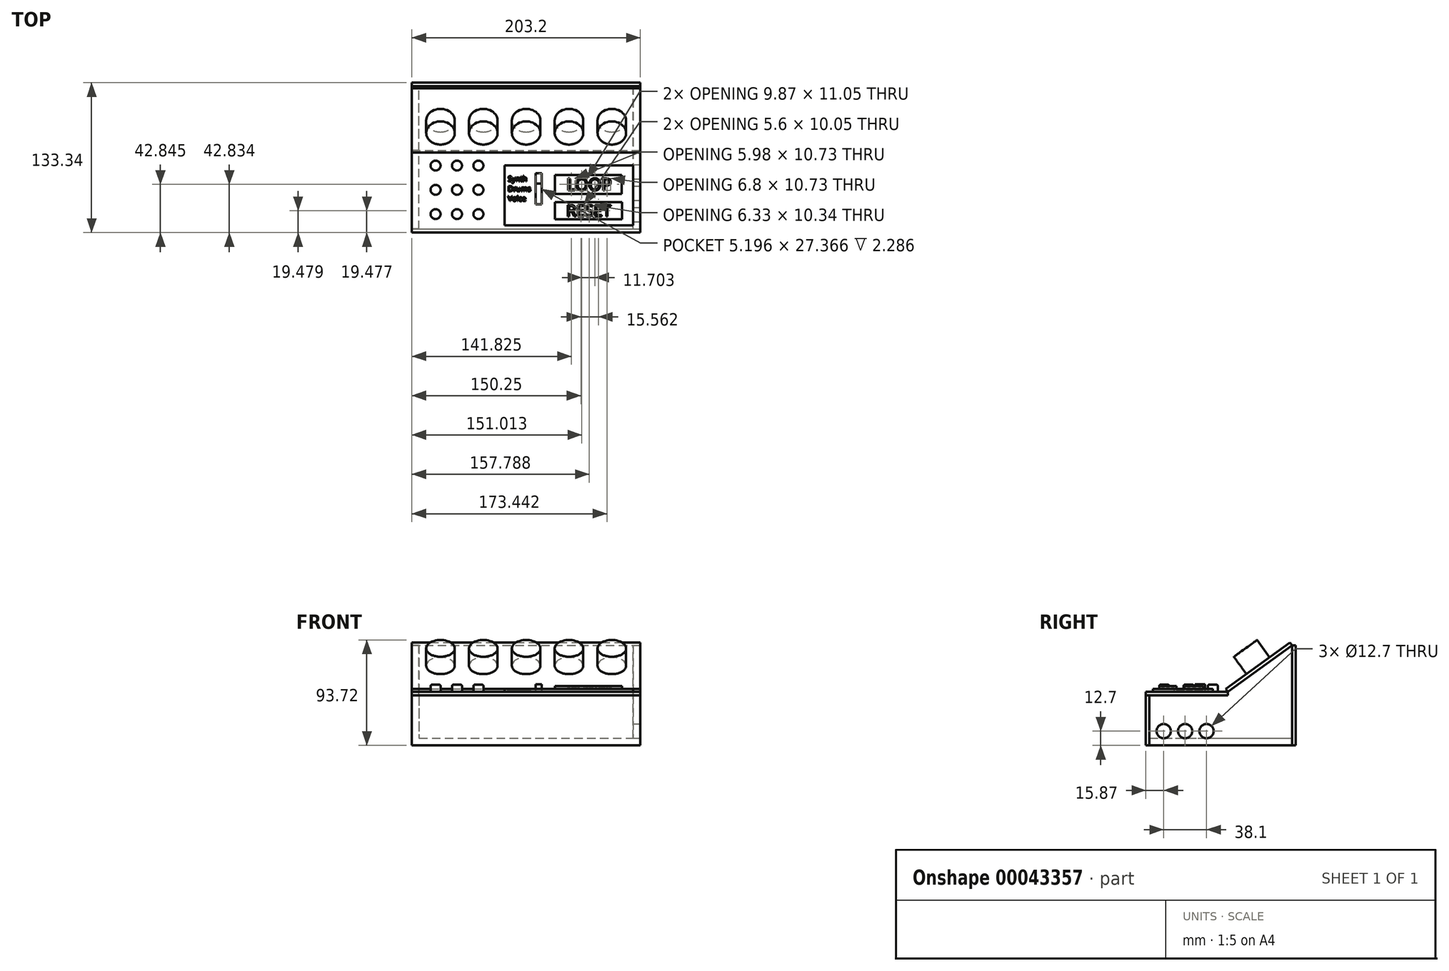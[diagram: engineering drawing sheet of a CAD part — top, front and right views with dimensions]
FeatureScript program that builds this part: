
annotation { "Feature Type Name" : "Feature", "Feature Type Description" : "" }
export const myFeature = defineFeature(function(context is Context, id is Id, definition is map)
    precondition{}
    {
        {
            var Q0;
            Q0=qCreatedBy(makeId("Top.planeOp"),FACE);
            var sketch = newSketch(context, id + "F0", { "sketchPlane" : qUnion([Q0])});
            skLineSegment(sketch, "E0.rect.bottom", {"start": v(-101.6, -63.5) * mm, "end": v(101.6, -63.5) * mm});
            skLineSegment(sketch, "E0.rect.top", {"start": v(-101.6, 63.5) * mm, "end": v(101.6, 63.5) * mm});
            skLineSegment(sketch, "E0.rect.left", {"start": v(-101.6, -63.5) * mm, "end": v(-101.6, 63.5) * mm});
            skLineSegment(sketch, "E0.rect.right", {"start": v(101.6, -63.5) * mm, "end": v(101.6, 63.5) * mm});
            skPoint(sketch, "E0.rect.middle", {"position": v(0, 0) * mm});
            skSolve(sketch);
        }
        {
            var Q0;
            Q0 = qSketchRegion(id + "F0", true);
            extrude(context, id + "F1", {"entities" : qUnion([Q0]), "depth" : 6.35 * mm});
        }
        {
            var Q0;
            Q0=makeQuery(id+"F1.opExtrude","SWEPT_FACE",FACE,{"disambiguationData":[OSD([sQuery(id+"F0.wireOp",EDGE,"E0.rect.left")])]});
            var sketch = newSketch(context, id + "F2", { "sketchPlane" : qUnion([Q0])});
            skLineSegment(sketch, "E1", {"start": v(-63.5, 6.35) * mm, "end": v(0, 6.35) * mm});
            skLineSegment(sketch, "E2", {"start": v(0, 6.35) * mm, "end": v(0, 44.45) * mm});
            skLineSegment(sketch, "E3", {"start": v(0, 44.45) * mm, "end": v(-6.35, 44.45) * mm});
            skLineSegment(sketch, "E4", {"start": v(-6.35, 44.45) * mm, "end": v(-6.35, 47.63) * mm});
            skLineSegment(sketch, "E5", {"start": v(-6.35, 47.62) * mm, "end": v(-63.5, 88.9) * mm});
            skLineSegment(sketch, "E6", {"start": v(-63.5, 88.9) * mm, "end": v(-63.5, 6.35) * mm});
            skLineSegment(sketch, "E7", {"start": v(0, 44.45) * mm, "end": v(63.5, 44.45) * mm});
            skLineSegment(sketch, "E8", {"start": v(63.5, 44.45) * mm, "end": v(63.5, 6.35) * mm});
            skLineSegment(sketch, "E9", {"start": v(63.5, 6.35) * mm, "end": v(0, 6.35) * mm});
            skSolve(sketch);
        }
        {
            var Q0;
            Q0 = qSketchRegion(id + "F2", true);
            extrude(context, id + "F3", {"entities" : qUnion([Q0]), "operationType" : NewBodyOperationType.ADD, "oppositeDirection" : true, "depth" : 6.35 * mm});
        }
        {
            var Q0;
            Q0=makeQuery(id+"F1.opExtrude","SWEPT_FACE",FACE,{"disambiguationData":[OSD([sQuery(id+"F0.wireOp",EDGE,"E0.rect.right")])]});
            var sketch = newSketch(context, id + "F4", { "sketchPlane" : qUnion([Q0])});
            skLineSegment(sketch, "E10.0.0", {"start": v(63.5, 6.35) * mm, "end": v(63.5, 6.35) * mm});
            skLineSegment(sketch, "E11.0.0", {"start": v(-63.5, 6.35) * mm, "end": v(63.5, 6.35) * mm});
            skLineSegment(sketch, "E11.0.1", {"start": v(63.5, 6.35) * mm, "end": v(63.5, 88.9) * mm});
            skLineSegment(sketch, "E11.0.2", {"start": v(63.5, 88.9) * mm, "end": v(6.35, 47.62) * mm});
            skLineSegment(sketch, "E11.0.3", {"start": v(6.35, 47.62) * mm, "end": v(6.35, 44.45) * mm});
            skLineSegment(sketch, "E11.0.4", {"start": v(6.35, 44.45) * mm, "end": v(-63.5, 44.45) * mm});
            skLineSegment(sketch, "E11.0.5", {"start": v(-63.5, 44.45) * mm, "end": v(-63.5, 6.35) * mm});
            skSolve(sketch);
        }
        {
            var Q0;
            Q0 = qSketchRegion(id + "F4", true);
            extrude(context, id + "F5", {"entities" : qUnion([Q0]), "operationType" : NewBodyOperationType.ADD, "oppositeDirection" : true, "depth" : 6.35 * mm});
        }
        {
            var Q0;
            Q0=makeQuery(id+"F3.opExtrude","SWEPT_FACE",FACE,{"disambiguationData":[OSD([sQuery(id+"F2.wireOp",EDGE,"E5")])]});
            var sketch = newSketch(context, id + "F6", { "sketchPlane" : qUnion([Q0])});
            skLineSegment(sketch, "E12", {"start": v(-101.6, 103.53) * mm, "end": v(101.6, 103.53) * mm});
            skLineSegment(sketch, "E13", {"start": v(-101.6, 103.53) * mm, "end": v(-101.6, 33.03) * mm});
            skLineSegment(sketch, "E14", {"start": v(-101.6, 33.03) * mm, "end": v(101.6, 33.03) * mm});
            skLineSegment(sketch, "E15", {"start": v(101.6, 33.03) * mm, "end": v(101.6, 103.53) * mm});
            skSolve(sketch);
        }
        {
            var Q0;
            Q0 = qSketchRegion(id + "F6", true);
            extrude(context, id + "F7", {"entities" : qUnion([Q0]), "depth" : 3.17 * mm});
        }
        {
            var Q0;
            Q0=makeQuery(id+"F3.opExtrude","SWEPT_FACE",FACE,{"disambiguationData":[OSD([sQuery(id+"F2.wireOp",EDGE,"E3"),sQuery(id+"F2.wireOp",EDGE,"E7")])]});
            var sketch = newSketch(context, id + "F8", { "sketchPlane" : qUnion([Q0])});
            skLineSegment(sketch, "E16", {"start": v(-101.6, 6.35) * mm, "end": v(101.6, 6.35) * mm});
            skLineSegment(sketch, "E17", {"start": v(101.6, 6.35) * mm, "end": v(101.6, -63.5) * mm});
            skLineSegment(sketch, "E18", {"start": v(-101.6, 6.35) * mm, "end": v(-101.6, -66.68) * mm});
            skLineSegment(sketch, "E19", {"start": v(-101.6, -66.68) * mm, "end": v(101.6, -66.67) * mm});
            skLineSegment(sketch, "E20", {"start": v(101.6, -66.67) * mm, "end": v(101.6, -63.5) * mm});
            skSolve(sketch);
        }
        {
            var Q0;
            Q0 = qSketchRegion(id + "F8", true);
            extrude(context, id + "F9", {"entities" : qUnion([Q0]), "depth" : 3.17 * mm});
        }
        {
            var Q0;
            Q0=makeQuery(id+"F5.boolean.opBoolean","MERGE",FACE,{"derivedFrom":[makeQuery(id+"F3.boolean.opBoolean","MERGE",FACE,{"derivedFrom":[makeQuery(id+"F1.opExtrude","SWEPT_FACE",FACE,{"disambiguationData":[OSD([sQuery(id+"F0.wireOp",EDGE,"E0.rect.bottom")])]}),makeQuery(id+"F3.opExtrude","SWEPT_FACE",FACE,{"disambiguationData":[OSD([sQuery(id+"F2.wireOp",EDGE,"E8")])]})]}),makeQuery(id+"F5.opExtrude","SWEPT_FACE",FACE,{"disambiguationData":[OSD([sQuery(id+"F4.wireOp",EDGE,"E11.0.5")])]})]});
            var sketch = newSketch(context, id + "F10", { "sketchPlane" : qUnion([Q0])});
            skLineSegment(sketch, "E21.bottom", {"start": v(-101.6, 0) * mm, "end": v(101.6, 0) * mm});
            skLineSegment(sketch, "E21.top", {"start": v(-101.6, 44.45) * mm, "end": v(101.6, 44.45) * mm});
            skLineSegment(sketch, "E21.left", {"start": v(-101.6, 0) * mm, "end": v(-101.6, 44.45) * mm});
            skLineSegment(sketch, "E21.right", {"start": v(101.6, 0) * mm, "end": v(101.6, 44.45) * mm});
            skSolve(sketch);
        }
        {
            var Q0;
            Q0 = qSketchRegion(id + "F10", true);
            extrude(context, id + "F11", {"entities" : qUnion([Q0]), "depth" : 3.17 * mm});
        }
        {
            var Q0;
            Q0=makeQuery(id+"F5.boolean.opBoolean","MERGE",FACE,{"derivedFrom":[makeQuery(id+"F3.boolean.opBoolean","MERGE",FACE,{"derivedFrom":[makeQuery(id+"F1.opExtrude","SWEPT_FACE",FACE,{"disambiguationData":[OSD([sQuery(id+"F0.wireOp",EDGE,"E0.rect.top")])]}),makeQuery(id+"F3.opExtrude","SWEPT_FACE",FACE,{"disambiguationData":[OSD([sQuery(id+"F2.wireOp",EDGE,"E6")])]})]}),makeQuery(id+"F5.opExtrude","SWEPT_FACE",FACE,{"disambiguationData":[OSD([sQuery(id+"F4.wireOp",EDGE,"E11.0.1")])]})]});
            var sketch = newSketch(context, id + "F12", { "sketchPlane" : qUnion([Q0])});
            skLineSegment(sketch, "E22.bottom", {"start": v(-101.6, 0) * mm, "end": v(101.6, 0) * mm});
            skLineSegment(sketch, "E22.top", {"start": v(-101.6, 88.9) * mm, "end": v(101.6, 88.9) * mm});
            skLineSegment(sketch, "E22.left", {"start": v(-101.6, 0) * mm, "end": v(-101.6, 88.9) * mm});
            skLineSegment(sketch, "E22.right", {"start": v(101.6, 0) * mm, "end": v(101.6, 88.9) * mm});
            skSolve(sketch);
        }
        {
            var Q0;
            Q0 = qSketchRegion(id + "F12", true);
            extrude(context, id + "F13", {"entities" : qUnion([Q0]), "depth" : 3.17 * mm});
        }
        {
            var Q0;
            Q0=makeQuery(id+"F7.opExtrude","CAP_FACE",FACE,{"disambiguationData":[OSD([sQuery(id+"F6.wireOp",EDGE,"E12"),sQuery(id+"F6.wireOp",EDGE,"E13"),sQuery(id+"F6.wireOp",EDGE,"E14"),sQuery(id+"F6.wireOp",EDGE,"E15")])],"isStart":false});
            var sketch = newSketch(context, id + "F14", { "sketchPlane" : qUnion([Q0])});
            skCircle(sketch, "E23", {"center": v(76.2, 68.28) * mm, "radius": 12.7 * mm});
            skPoint(sketch, "E23.centerSnap0", {"position": v(101.6, 68.28) * mm});
            skCircle(sketch, "E24", {"center": v(38.1, 68.28) * mm, "radius": 12.7 * mm});
            skCircle(sketch, "E25", {"center": v(0, 68.28) * mm, "radius": 12.7 * mm});
            skCircle(sketch, "E26", {"center": v(-38.1, 68.28) * mm, "radius": 12.7 * mm});
            skCircle(sketch, "E27", {"center": v(-76.2, 68.28) * mm, "radius": 12.7 * mm});
            skSolve(sketch);
        }
        {
            var Q0;
            Q0 = qSketchRegion(id + "F14", true);
            extrude(context, id + "F15", {"entities" : qUnion([Q0]), "depth" : 19.05 * mm});
        }
        {
            var Q0;
            Q0=makeQuery(id+"F5.boolean.opBoolean","MERGE",FACE,{"derivedFrom":[makeQuery(id+"F1.opExtrude","SWEPT_FACE",FACE,{"disambiguationData":[OSD([sQuery(id+"F0.wireOp",EDGE,"E0.rect.right")])]}),makeQuery(id+"F5.opExtrude","CAP_FACE",FACE,{"disambiguationData":[OSD([sQuery(id+"F4.wireOp",EDGE,"E11.0.0"),sQuery(id+"F4.wireOp",EDGE,"E11.0.1"),sQuery(id+"F4.wireOp",EDGE,"E11.0.2"),sQuery(id+"F4.wireOp",EDGE,"E11.0.3"),sQuery(id+"F4.wireOp",EDGE,"E11.0.4"),sQuery(id+"F4.wireOp",EDGE,"E11.0.5")])],"isStart":true})]});
            var sketch = newSketch(context, id + "F16", { "sketchPlane" : qUnion([Q0])});
            skCircle(sketch, "E28", {"center": v(-50.8, 12.7) * mm, "radius": 6.35 * mm});
            skCircle(sketch, "E29", {"center": v(-31.75, 12.7) * mm, "radius": 6.35 * mm});
            skCircle(sketch, "E30", {"center": v(-12.7, 12.7) * mm, "radius": 6.35 * mm});
            skSolve(sketch);
        }
        {
            var Q0;
            Q0 = qSketchRegion(id + "F16", true);
            extrude(context, id + "F17", {"entities" : qUnion([Q0]), "operationType" : NewBodyOperationType.REMOVE, "oppositeDirection" : true, "depth" : 25.4 * mm});
        }
        {
            var Q0;
            Q0=makeQuery(id+"F9.opExtrude","CAP_FACE",FACE,{"disambiguationData":[OSD([sQuery(id+"F8.wireOp",EDGE,"E16"),sQuery(id+"F8.wireOp",EDGE,"E17"),sQuery(id+"F8.wireOp",EDGE,"E18"),sQuery(id+"F8.wireOp",EDGE,"E19"),sQuery(id+"F8.wireOp",EDGE,"E20")])],"isStart":false});
            var sketch = newSketch(context, id + "F18", { "sketchPlane" : qUnion([Q0])});
            skCircle(sketch, "E31", {"center": v(-63.5, -34.93) * mm, "radius": 26.07 * mm});
            skSolve(sketch);
        }
        {
            var Q0;
            Q0 = qSketchRegion(id + "F18", true);
            extrude(context, id + "F19", {"entities" : qUnion([Q0]), "depth" : 6.35 * mm});
        }
        {
            var Q0;
            Q0=makeQuery(id+"F19.opExtrude","CAP_EDGE",EDGE,{"disambiguationData":[OSD([sQuery(id+"F18.wireOp",EDGE,"E31")])],"isStart":false});
            fillet(context, id + "F20", {"entities" : qUnion([Q0]), "radius" : 6.35 * mm, "tangentPropagation" : true, "allowEdgeOverflow" : false});
        }
        {
            var Q0;
            Q0=makeQuery(id+"F9.opExtrude","CAP_FACE",FACE,{"disambiguationData":[OSD([sQuery(id+"F8.wireOp",EDGE,"E16"),sQuery(id+"F8.wireOp",EDGE,"E17"),sQuery(id+"F8.wireOp",EDGE,"E18"),sQuery(id+"F8.wireOp",EDGE,"E19"),sQuery(id+"F8.wireOp",EDGE,"E20")])],"isStart":false});
            var sketch = newSketch(context, id + "F21", { "sketchPlane" : qUnion([Q0])});
            skLineSegment(sketch, "E32.rect.bottom", {"start": v(95.25, -60.32) * mm, "end": v(-19.05, -60.32) * mm});
            skLineSegment(sketch, "E32.rect.top", {"start": v(95.25, -6.98) * mm, "end": v(-19.05, -6.98) * mm});
            skLineSegment(sketch, "E32.rect.left", {"start": v(95.25, -60.32) * mm, "end": v(95.25, -6.98) * mm});
            skLineSegment(sketch, "E32.rect.right", {"start": v(-19.05, -60.32) * mm, "end": v(-19.05, -6.98) * mm});
            skPoint(sketch, "E32.rect.middle", {"position": v(38.1, -33.65) * mm});
            skSolve(sketch);
        }
        {
            var Q0;
            Q0 = qSketchRegion(id + "F21", true);
            extrude(context, id + "F22", {"entities" : qUnion([Q0]), "operationType" : NewBodyOperationType.ADD, "depth" : 2.54 * mm});
        }
        {
            var Q0;
            Q0=makeQuery(id+"F22.opExtrude","CAP_FACE",FACE,{"disambiguationData":[OSD([sQuery(id+"F21.wireOp",EDGE,"E32.rect.bottom"),sQuery(id+"F21.wireOp",EDGE,"E32.rect.top"),sQuery(id+"F21.wireOp",EDGE,"E32.rect.left"),sQuery(id+"F21.wireOp",EDGE,"E32.rect.right")])],"isStart":false});
            var sketch = newSketch(context, id + "F23", { "sketchPlane" : qUnion([Q0])});
            skText(sketch, "E33", { "text": "Synth\nDrums\nVoice", "fontName": "OpenSans-Regular.ttf"});
            const initialGuessF23  = {"E33": [-0.0162, -0.02115, 1, 0, 0.00466]};
            skSetInitialGuess(sketch, initialGuessF23);
            skSolve(sketch);
        }
        {
            var Q0;
            Q0 = qSketchRegion(id + "F23", true);
            extrude(context, id + "F24", {"entities" : qUnion([Q0]), "operationType" : NewBodyOperationType.REMOVE, "oppositeDirection" : true, "depth" : 1.27 * mm});
        }
        {
            var Q0;
            {var subQ0=sQuery(id+"F21.wireOp",EDGE,"E32.rect.bottom");var subQ1=sQuery(id+"F21.wireOp",EDGE,"E32.rect.top");var subQ2=sQuery(id+"F21.wireOp",EDGE,"E32.rect.left");var subQ3=sQuery(id+"F21.wireOp",EDGE,"E32.rect.right");Q0=makeQuery(id+"F24.boolean.opBoolean","SPLIT",FACE,{"disambiguationData":[TD([makeQuery(id+"F22.opExtrude","SWEPT_FACE",FACE,{"disambiguationData":[OSD([subQ0])]})])],"derivedFrom":makeQuery(id+"F22.opExtrude","CAP_FACE",FACE,{"disambiguationData":[OSD([subQ0,subQ1,subQ2,subQ3])],"isStart":false})});}
            var sketch = newSketch(context, id + "F25", { "sketchPlane" : qUnion([Q0])});
            skLineSegment(sketch, "E34.rect.bottom", {"start": v(8.48, -14.05) * mm, "end": v(13.67, -14.05) * mm});
            skLineSegment(sketch, "E34.rect.top", {"start": v(8.48, -41.41) * mm, "end": v(13.67, -41.41) * mm});
            skLineSegment(sketch, "E34.rect.left", {"start": v(8.48, -14.05) * mm, "end": v(8.48, -41.41) * mm});
            skLineSegment(sketch, "E34.rect.right", {"start": v(13.67, -14.05) * mm, "end": v(13.67, -41.41) * mm});
            skPoint(sketch, "E34.rect.middle", {"position": v(11.08, -27.73) * mm});
            skSolve(sketch);
        }
        {
            var Q0;
            Q0 = qSketchRegion(id + "F25", true);
            extrude(context, id + "F26", {"entities" : qUnion([Q0]), "operationType" : NewBodyOperationType.REMOVE, "oppositeDirection" : true, "depth" : 2.3 * mm});
        }
        {
            var Q0;
            Q0=makeQuery(id+"F26.boolean.opBoolean","COPY",FACE,{"derivedFrom":makeQuery(id+"F26.opExtrude","CAP_FACE",FACE,{"disambiguationData":[OSD([sQuery(id+"F25.wireOp",EDGE,"E34.rect.bottom"),sQuery(id+"F25.wireOp",EDGE,"E34.rect.top"),sQuery(id+"F25.wireOp",EDGE,"E34.rect.left"),sQuery(id+"F25.wireOp",EDGE,"E34.rect.right")])],"isStart":false})});
            var sketch = newSketch(context, id + "F27", { "sketchPlane" : qUnion([Q0])});
            skLineSegment(sketch, "E35.bottom", {"start": v(8.48, -14.05) * mm, "end": v(13.67, -14.05) * mm});
            skLineSegment(sketch, "E35.top", {"start": v(8.48, -23.05) * mm, "end": v(13.67, -23.05) * mm});
            skLineSegment(sketch, "E35.left", {"start": v(8.48, -14.05) * mm, "end": v(8.48, -23.05) * mm});
            skLineSegment(sketch, "E35.right", {"start": v(13.67, -14.05) * mm, "end": v(13.67, -23.05) * mm});
            skSolve(sketch);
        }
        {
            var Q0;
            Q0 = qSketchRegion(id + "F27", true);
            extrude(context, id + "F28", {"entities" : qUnion([Q0]), "depth" : 6.35 * mm});
        }
        {
            var Q0;
            {var subQ0=sQuery(id+"F21.wireOp",EDGE,"E32.rect.bottom");var subQ1=sQuery(id+"F21.wireOp",EDGE,"E32.rect.top");var subQ2=sQuery(id+"F21.wireOp",EDGE,"E32.rect.left");var subQ3=sQuery(id+"F21.wireOp",EDGE,"E32.rect.right");Q0=makeQuery(id+"F24.boolean.opBoolean","SPLIT",FACE,{"disambiguationData":[TD([makeQuery(id+"F22.opExtrude","SWEPT_FACE",FACE,{"disambiguationData":[OSD([subQ0])]})])],"derivedFrom":makeQuery(id+"F22.opExtrude","CAP_FACE",FACE,{"disambiguationData":[OSD([subQ0,subQ1,subQ2,subQ3])],"isStart":false})});}
            var sketch = newSketch(context, id + "F29", { "sketchPlane" : qUnion([Q0])});
            skLineSegment(sketch, "E36.bottom", {"start": v(25.45, -15.63) * mm, "end": v(85.06, -15.63) * mm});
            skLineSegment(sketch, "E36.top", {"start": v(25.45, -32.46) * mm, "end": v(85.06, -32.46) * mm});
            skLineSegment(sketch, "E36.left", {"start": v(25.45, -15.63) * mm, "end": v(25.45, -32.46) * mm});
            skLineSegment(sketch, "E36.right", {"start": v(85.06, -15.63) * mm, "end": v(85.06, -32.46) * mm});
            skLineSegment(sketch, "E37.bottom", {"start": v(25.45, -39.5) * mm, "end": v(85.4, -39.5) * mm});
            skLineSegment(sketch, "E37.top", {"start": v(25.45, -54.8) * mm, "end": v(85.4, -54.8) * mm});
            skLineSegment(sketch, "E37.left", {"start": v(25.45, -39.5) * mm, "end": v(25.45, -54.8) * mm});
            skLineSegment(sketch, "E37.right", {"start": v(85.4, -39.5) * mm, "end": v(85.4, -54.8) * mm});
            skText(sketch, "E38", { "text": "LOOP", "fontName": "OpenSans-Regular.ttf"});
            skText(sketch, "E39", { "text": "RESET", "fontName": "OpenSans-Regular.ttf"});
            const initialGuessF29  = {"E38": [0.03576, -0.0292, 1, 0, 0.01082], "E39": [0.03576, -0.05222, 1, 0, 0.01014]};
            skSetInitialGuess(sketch, initialGuessF29);
            skSolve(sketch);
        }
        {
            var Q0;
            Q0 = qSketchRegion(id + "F29", true);
            var Q1;
            Q1=makeQuery(id+"F29.imprint","IMPRINT",FACE,{"disambiguationData":[TD([[makeQuery(id+"F29.imprint","IMPRINT",EDGE,{"derivedFrom":sQuery(id+"F29.wireOp",EDGE,"E38.sketch_text.stroke-46")}),1.0]])]});
            var Q2;
            Q2=makeQuery(id+"F29.imprint","IMPRINT",FACE,{"disambiguationData":[TD([[makeQuery(id+"F29.imprint","IMPRINT",EDGE,{"derivedFrom":sQuery(id+"F29.wireOp",EDGE,"E38.sketch_text.stroke-30")}),1.0]])]});
            var Q3;
            Q3=makeQuery(id+"F29.imprint","IMPRINT",FACE,{"disambiguationData":[TD([[makeQuery(id+"F29.imprint","IMPRINT",EDGE,{"derivedFrom":sQuery(id+"F29.wireOp",EDGE,"E38.sketch_text.stroke-14")}),1.0]])]});
            var Q4;
            Q4=makeQuery(id+"F29.imprint","IMPRINT",FACE,{"disambiguationData":[TD([[makeQuery(id+"F29.imprint","IMPRINT",EDGE,{"derivedFrom":sQuery(id+"F29.wireOp",EDGE,"E39.sketch_text.stroke-11")}),1.0]])]});
            extrude(context, id + "F30", {"entities" : qUnion([Q0, Q1, Q2, Q3, Q4]), "depth" : 2.54 * mm});
        }
        {
            var Q0;
            Q0=makeQuery(id+"F19.opExtrude","SWEPT_BODY",BODY,{"disambiguationData":[OSD([sQuery(id+"F18.wireOp",EDGE,"E31")])]});
            deleteBodies(context, id + "F31", {"entities" : qUnion([Q0])});
        }
        {
            var Q0;
            Q0=makeQuery(id+"F9.opExtrude","CAP_FACE",FACE,{"disambiguationData":[OSD([sQuery(id+"F8.wireOp",EDGE,"E16"),sQuery(id+"F8.wireOp",EDGE,"E17"),sQuery(id+"F8.wireOp",EDGE,"E18"),sQuery(id+"F8.wireOp",EDGE,"E19"),sQuery(id+"F8.wireOp",EDGE,"E20")])],"isStart":false});
            var sketch = newSketch(context, id + "F32", { "sketchPlane" : qUnion([Q0])});
            skCircle(sketch, "E40", {"center": v(-61.52, -7.08) * mm, "radius": 4.45 * mm});
            skCircle(sketch, "E41", {"center": v(-42.47, -7.08) * mm, "radius": 4.45 * mm});
            skCircle(sketch, "E42", {"center": v(-80.57, -7.08) * mm, "radius": 4.45 * mm});
            skCircle(sketch, "E43", {"center": v(-80.57, -28.67) * mm, "radius": 4.45 * mm});
            skCircle(sketch, "E44", {"center": v(-61.52, -28.67) * mm, "radius": 4.45 * mm});
            skCircle(sketch, "E45", {"center": v(-42.47, -28.67) * mm, "radius": 4.45 * mm});
            skCircle(sketch, "E46", {"center": v(-80.57, -50.26) * mm, "radius": 4.45 * mm});
            skCircle(sketch, "E47", {"center": v(-61.52, -50.26) * mm, "radius": 4.45 * mm});
            skCircle(sketch, "E48", {"center": v(-42.47, -50.26) * mm, "radius": 4.45 * mm});
            skSolve(sketch);
        }
        {
            var Q0;
            Q0 = qSketchRegion(id + "F32", true);
            extrude(context, id + "F33", {"entities" : qUnion([Q0]), "depth" : 6.35 * mm});
        }
        {
            var Q0;
            Q0=makeQuery(id+"F33.opExtrude","CAP_FACE",FACE,{"disambiguationData":[OSD([sQuery(id+"F32.wireOp",EDGE,"E43")])],"isStart":false});
            var Q1;
            Q1=makeQuery(id+"F33.opExtrude","CAP_FACE",FACE,{"disambiguationData":[OSD([sQuery(id+"F32.wireOp",EDGE,"E46")])],"isStart":false});
            var Q2;
            Q2=makeQuery(id+"F33.opExtrude","CAP_FACE",FACE,{"disambiguationData":[OSD([sQuery(id+"F32.wireOp",EDGE,"E47")])],"isStart":false});
            var Q3;
            Q3=makeQuery(id+"F33.opExtrude","CAP_FACE",FACE,{"disambiguationData":[OSD([sQuery(id+"F32.wireOp",EDGE,"E44")])],"isStart":false});
            var Q4;
            Q4=makeQuery(id+"F33.opExtrude","CAP_FACE",FACE,{"disambiguationData":[OSD([sQuery(id+"F32.wireOp",EDGE,"E42")])],"isStart":false});
            var Q5;
            Q5=makeQuery(id+"F33.opExtrude","CAP_FACE",FACE,{"disambiguationData":[OSD([sQuery(id+"F32.wireOp",EDGE,"E40")])],"isStart":false});
            var Q6;
            Q6=makeQuery(id+"F33.opExtrude","CAP_FACE",FACE,{"disambiguationData":[OSD([sQuery(id+"F32.wireOp",EDGE,"E41")])],"isStart":false});
            var Q7;
            Q7=makeQuery(id+"F33.opExtrude","CAP_FACE",FACE,{"disambiguationData":[OSD([sQuery(id+"F32.wireOp",EDGE,"E45")])],"isStart":false});
            var Q8;
            Q8=makeQuery(id+"F33.opExtrude","CAP_FACE",FACE,{"disambiguationData":[OSD([sQuery(id+"F32.wireOp",EDGE,"E48")])],"isStart":false});
            fillet(context, id + "F34", {"entities" : qUnion([Q0, Q1, Q2, Q3, Q4, Q5, Q6, Q7, Q8]), "radius" : 1.27 * mm, "tangentPropagation" : true, "allowEdgeOverflow" : false});
        }
    });
